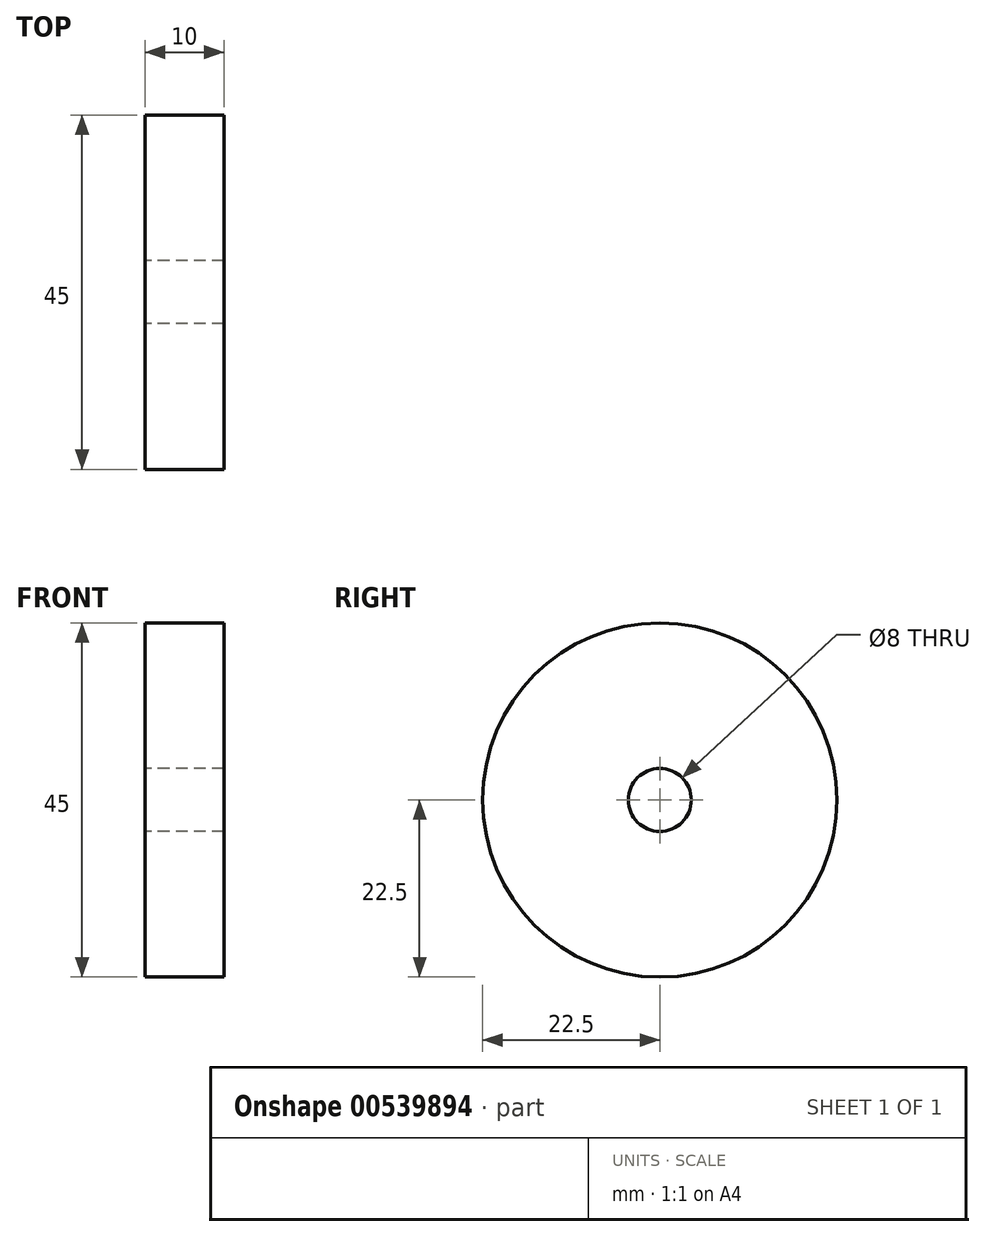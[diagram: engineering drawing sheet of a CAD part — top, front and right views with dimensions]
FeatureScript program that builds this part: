
annotation { "Feature Type Name" : "Feature", "Feature Type Description" : "" }
export const myFeature = defineFeature(function(context is Context, id is Id, definition is map)
    precondition{}
    {
        {
            var Q0;
            Q0=qCreatedBy(makeId("Right.planeOp"),FACE);
            var sketch = newSketch(context, id + "F0", { "sketchPlane" : qUnion([Q0])});
            skCircle(sketch, "E0", {"center": v(0, 0) * mm, "radius": 4 * mm});
            skCircle(sketch, "E1", {"center": v(0, 0) * mm, "radius": 22.5 * mm});
            skSolve(sketch);
        }
        {
            var Q0;
            Q0=makeQuery(id+"F0.imprint","IMPRINT",FACE,{"disambiguationData":[TD([[makeQuery(id+"F0.imprint","IMPRINT",EDGE,{"derivedFrom":sQuery(id+"F0.wireOp",EDGE,"E0")}),-1.0]])]});
            extrude(context, id + "F1", {"entities" : qUnion([Q0]), "depth" : 10 * mm, "offsetDistance" : 25 * mm});
        }
    });
